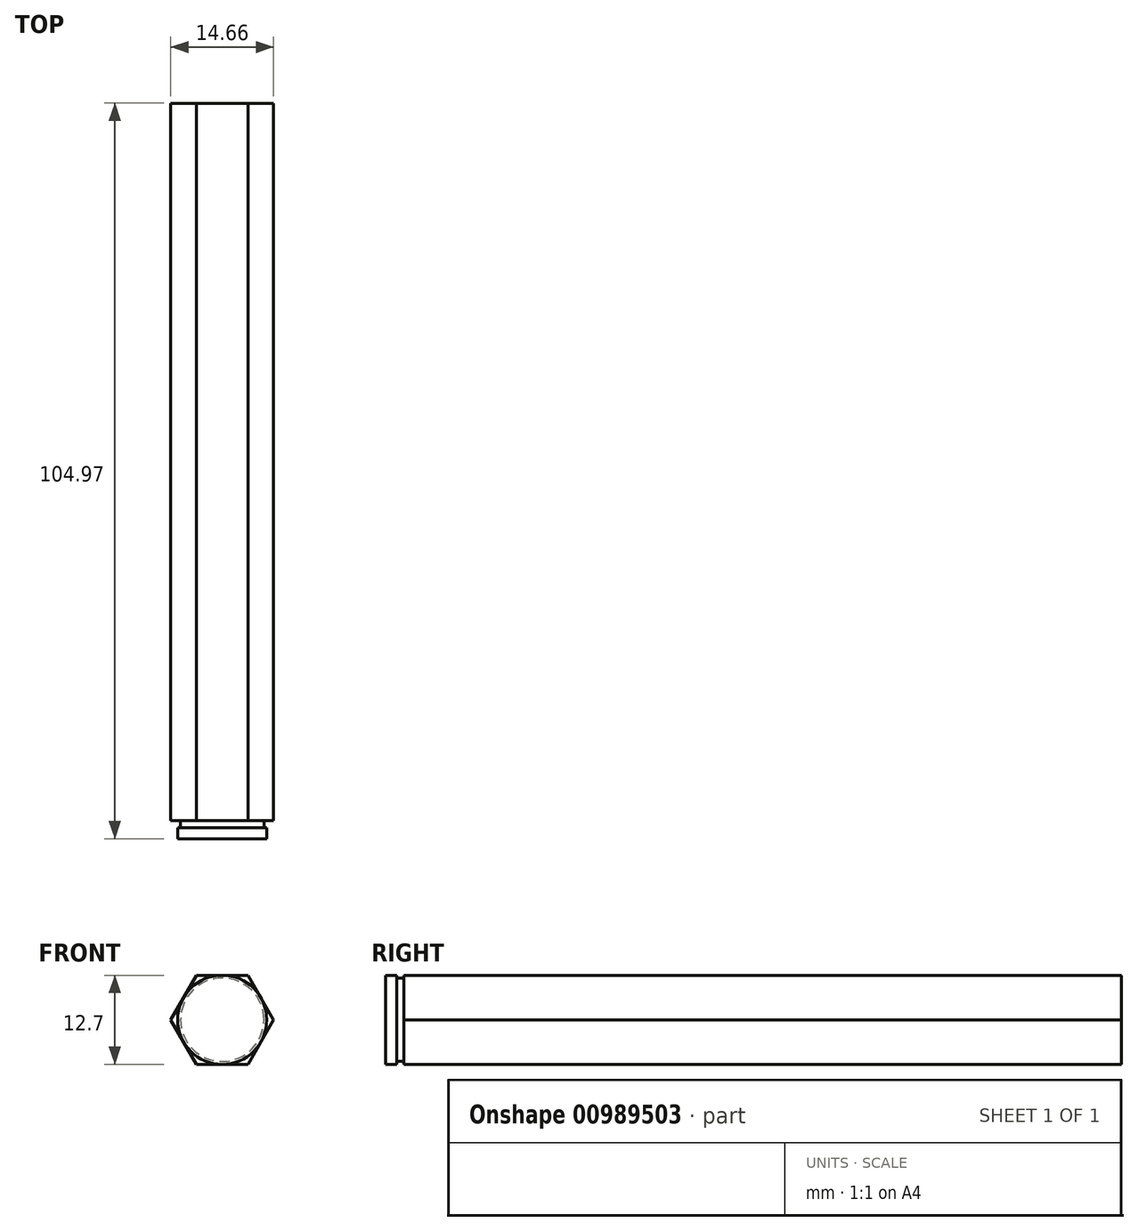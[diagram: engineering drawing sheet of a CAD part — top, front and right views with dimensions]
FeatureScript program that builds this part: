
annotation { "Feature Type Name" : "Feature", "Feature Type Description" : "" }
export const myFeature = defineFeature(function(context is Context, id is Id, definition is map)
    precondition{}
    {
        {
            var Q0;
            Q0=qCreatedBy(makeId("Front.planeOp"),FACE);
            var sketch = newSketch(context, id + "F0", { "sketchPlane" : qUnion([Q0])});
            skCircle(sketch, "E0.cCircle", {"center": v(0, 0) * mm, "radius": 6.35 * mm, "construction": true});
            skLineSegment(sketch, "E0.0", {"start": v(-3.67, 6.35) * mm, "end": v(3.67, 6.35) * mm});
            skLineSegment(sketch, "E0.1", {"start": v(3.67, 6.35) * mm, "end": v(7.33, 0) * mm});
            skLineSegment(sketch, "E0.2", {"start": v(7.33, 0) * mm, "end": v(3.67, -6.35) * mm});
            skLineSegment(sketch, "E0.3", {"start": v(3.67, -6.35) * mm, "end": v(-3.67, -6.35) * mm});
            skLineSegment(sketch, "E0.4", {"start": v(-3.67, -6.35) * mm, "end": v(-7.33, 0) * mm});
            skLineSegment(sketch, "E0.5", {"start": v(-7.33, 0) * mm, "end": v(-3.67, 6.35) * mm});
            skPoint(sketch, "E0.0.midPoint", {"position": v(0, 6.35) * mm});
            skSolve(sketch);
        }
        {
            var Q0;
            Q0 = qSketchRegion(id + "F0", true);
            extrude(context, id + "F1", {"entities" : qUnion([Q0]), "depth" : 51.2 * mm, "offsetDistance" : 25.4 * mm, "hasSecondDirection" : true, "secondDirectionOppositeDirection" : true, "secondDirectionDepth" : 51.2 * mm});
        }
        {
            var Q0;
            Q0=makeQuery(id+"F1.opExtrude","CAP_FACE",FACE,{"disambiguationData":[OSD([sQuery(id+"F0.wireOp",EDGE,"E0.0"),sQuery(id+"F0.wireOp",EDGE,"E0.1"),sQuery(id+"F0.wireOp",EDGE,"E0.2"),sQuery(id+"F0.wireOp",EDGE,"E0.3"),sQuery(id+"F0.wireOp",EDGE,"E0.4"),sQuery(id+"F0.wireOp",EDGE,"E0.5")])],"isStart":false});
            var sketch = newSketch(context, id + "F2", { "sketchPlane" : qUnion([Q0])});
            skCircle(sketch, "E1", {"center": v(0, 0) * mm, "radius": 5.94 * mm});
            skSolve(sketch);
        }
        {
            var Q0;
            Q0 = qSketchRegion(id + "F2", true);
            extrude(context, id + "F3", {"entities" : qUnion([Q0]), "operationType" : NewBodyOperationType.ADD, "depth" : 1 * mm, "offsetDistance" : 25.4 * mm});
        }
        {
            var Q0;
            Q0=makeQuery(id+"F3.opExtrude","CAP_FACE",FACE,{"disambiguationData":[OSD([sQuery(id+"F2.wireOp",EDGE,"E1")])],"isStart":false});
            var sketch = newSketch(context, id + "F4", { "sketchPlane" : qUnion([Q0])});
            skCircle(sketch, "E2", {"center": v(0, 0) * mm, "radius": 6.35 * mm});
            skSolve(sketch);
        }
        {
            var Q0;
            Q0 = qSketchRegion(id + "F4", true);
            extrude(context, id + "F5", {"entities" : qUnion([Q0]), "operationType" : NewBodyOperationType.ADD, "depth" : 1.59 * mm, "offsetDistance" : 25.4 * mm});
        }
    });
